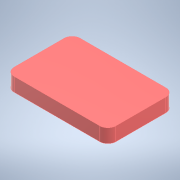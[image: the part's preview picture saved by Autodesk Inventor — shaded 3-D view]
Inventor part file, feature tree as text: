
AUTODESK INVENTOR PART (.ipt)
format: ipt  version: 2021 (Build 250183000, 183)  size: 112,640 bytes
history: native  units: mm
features: extrude x1, sketch x1
ambient origin geometry x8: Origin, YZ Plane, XZ Plane, XY Plane, X Axis, Y Axis, Z Axis, Center Point
bodies: Solid1 (feature_tree)
feature tree (2):
  extrude  "Extrusion1"  Depth=16.4mm
  sketch  "Sketch1"  dims[d0=25.25mm d1=16.4mm d2=3.4mm d3=0.0mm d4=2.0mm]
